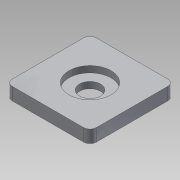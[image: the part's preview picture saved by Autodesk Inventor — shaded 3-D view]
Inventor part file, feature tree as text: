
AUTODESK INVENTOR PART (.ipt)
format: ipt  version: 2013 SP2 (Build 170200200, 200)  size: 97,280 bytes
history: native  units: mm
features: extrude x3, sketch x2, fillet x2
ambient origin geometry x8: Origin, YZ Plane, XZ Plane, XY Plane, X Axis, Y Axis, Z Axis, Center Point
bodies: Solid1 (feature_tree)
feature tree (7):
  extrude  "Extrusion1"  Depth=20.0mm
  sketch  "Sketch2"  dims[d2=3.0mm d3=0.0mm d4=5.0mm d5=10.0mm d6=3.0mm d7=0.0mm d8=1.5mm d9=0.0mm d10=1.5mm d11=1.5mm]
  extrude  "Extrusion2"  Depth=5.0mm
  extrude  "Extrusion3"  Depth=10.0mm
  fillet  "Fillet1"  Radius=3.0mm
  fillet  "Fillet2"  Radius=1.5mm
  sketch  "Sketch1"  dims[d0=20.0mm d1=20.0mm]
